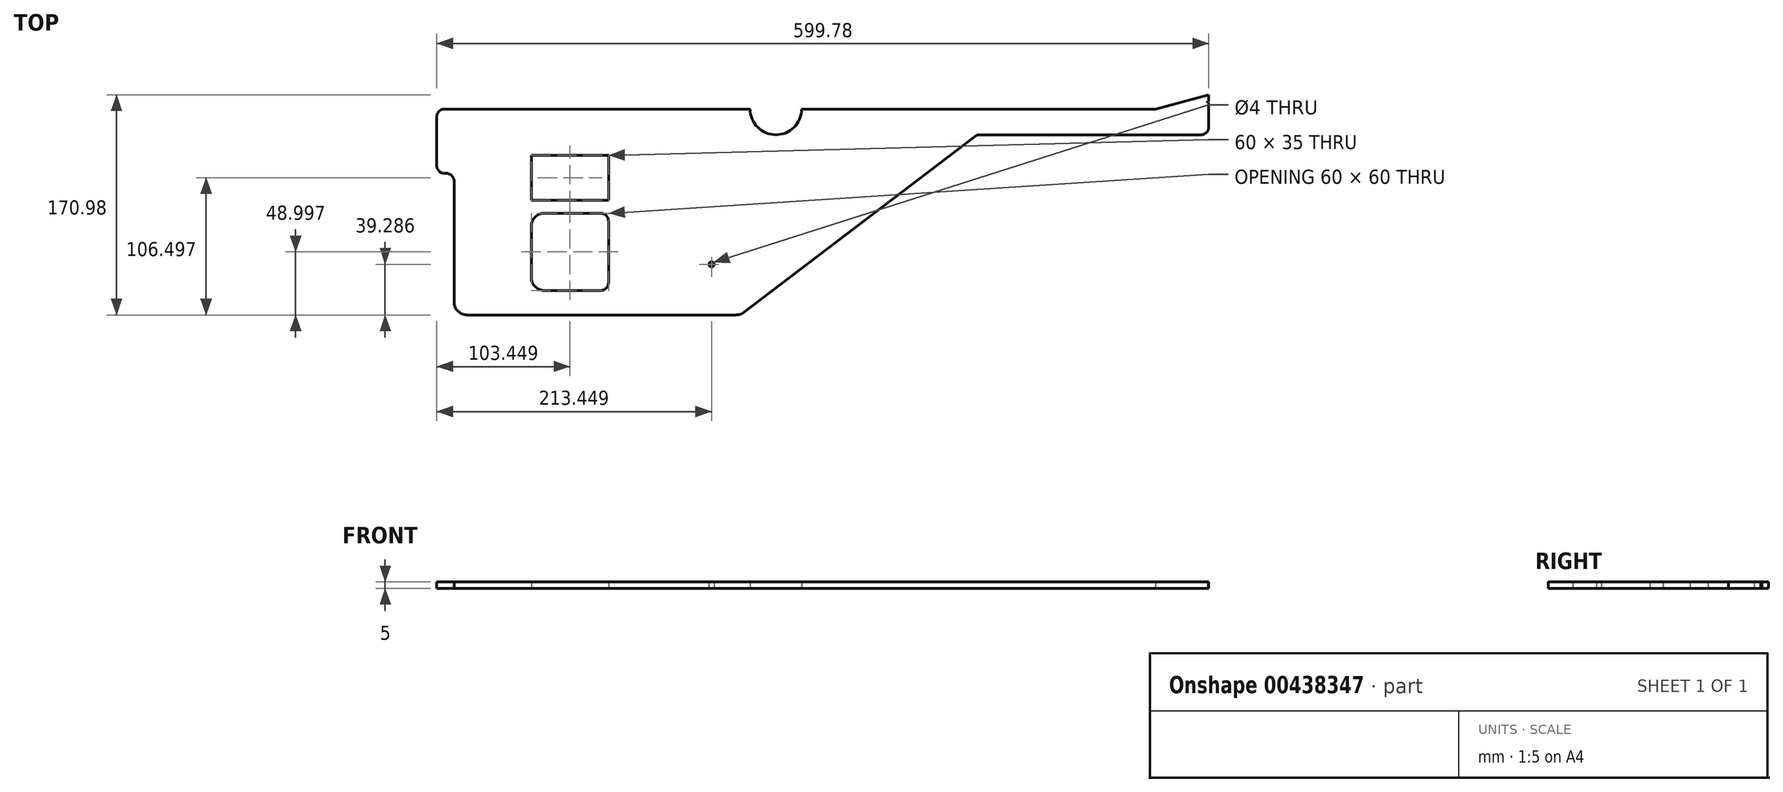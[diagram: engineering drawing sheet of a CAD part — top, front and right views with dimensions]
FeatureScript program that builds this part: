
annotation { "Feature Type Name" : "Feature", "Feature Type Description" : "" }
export const myFeature = defineFeature(function(context is Context, id is Id, definition is map)
    precondition{}
    {
        {
            var Q0;
            Q0=qCreatedBy(makeId("Top.planeOp"),FACE);
            var sketch = newSketch(context, id + "F0", { "sketchPlane" : qUnion([Q0])});
            skLineSegment(sketch, "E0", {"start": v(380.94, 53.83) * mm, "end": v(379.94, 53.83) * mm});
            skLineSegment(sketch, "E1", {"start": v(379.94, 53.83) * mm, "end": v(379.94, 54.83) * mm});
            skLineSegment(sketch, "E2", {"start": v(379.94, 54.83) * mm, "end": v(380.94, 54.83) * mm});
            skLineSegment(sketch, "E3", {"start": v(380.94, 54.83) * mm, "end": v(380.94, 59.83) * mm});
            skPoint(sketch, "E4", {"position": v(339.6, 48.83) * mm});
            skLineSegment(sketch, "E5", {"start": v(339.6, 48.83) * mm, "end": v(380.94, 59.83) * mm});
            skLineSegment(sketch, "E6", {"start": v(380.94, 53.83) * mm, "end": v(380.94, 34.83) * mm});
            skLineSegment(sketch, "E7", {"start": v(374.94, 28.83) * mm, "end": v(202.97, 28.83) * mm});
            skLineSegment(sketch, "E8", {"start": v(20, -109.1) * mm, "end": v(199.33, 27.6) * mm});
            skPoint(sketch, "E9.visualSharp", {"position": v(-218.84, 48.85) * mm});
            skPoint(sketch, "E10.visualSharp", {"position": v(17.31, -111.15) * mm});
            skArc(sketch, "E10.filletArc", {"start": v(13.94, -111.15) * mm, "mid": v(17.14, -110.63) * mm, "end": v(20, -109.1) * mm});
            skPoint(sketch, "E11.visualSharp", {"position": v(200.94, 28.83) * mm});
            skArc(sketch, "E11.filletArc", {"start": v(202.97, 28.83) * mm, "mid": v(201.05, 28.52) * mm, "end": v(199.33, 27.6) * mm});
            skPoint(sketch, "E12.visualSharp", {"position": v(380.94, 28.83) * mm});
            skArc(sketch, "E12.filletArc", {"start": v(374.94, 28.83) * mm, "mid": v(379.18, 30.6) * mm, "end": v(380.94, 34.83) * mm});
            skPoint(sketch, "E13", {"position": v(-5.4, -71.86) * mm});
            skCircle(sketch, "E14", {"center": v(-5.4, -71.86) * mm, "radius": 2 * mm});
            skPoint(sketch, "E15.visualSharp", {"position": v(20.24, -108.22) * mm});
            skLineSegment(sketch, "E16.bottom", {"start": v(-91.4, 12.85) * mm, "end": v(-145.4, 12.85) * mm});
            skLineSegment(sketch, "E16.top", {"start": v(-85.4, -22.15) * mm, "end": v(-145.4, -22.15) * mm});
            skLineSegment(sketch, "E16.left", {"start": v(-85.4, 6.85) * mm, "end": v(-85.4, -22.15) * mm});
            skLineSegment(sketch, "E16.right", {"start": v(-145.4, 12.85) * mm, "end": v(-145.4, -22.15) * mm});
            skLineSegment(sketch, "E17.bottom", {"start": v(-85.4, 12.85) * mm, "end": v(-145.4, 12.85) * mm});
            skLineSegment(sketch, "E17.top", {"start": v(-91.4, -22.15) * mm, "end": v(-145.4, -22.15) * mm});
            skLineSegment(sketch, "E17.left", {"start": v(-85.4, 12.85) * mm, "end": v(-85.4, -16.15) * mm});
            skArc(sketch, "E18.filletArc", {"start": v(-212.84, 48.85) * mm, "mid": v(-217.08, 47.09) * mm, "end": v(-218.84, 42.85) * mm});
            skArc(sketch, "E19", {"start": v(24.6, 48.84) * mm, "mid": v(44.6, 28.85) * mm, "end": v(64.6, 48.84) * mm});
            skLineSegment(sketch, "E20", {"start": v(-212.84, 48.85) * mm, "end": v(24.6, 48.84) * mm});
            skLineSegment(sketch, "E21", {"start": v(64.6, 48.84) * mm, "end": v(339.6, 48.83) * mm});
            skLineSegment(sketch, "E22.bottom", {"start": v(-91.4, -32.15) * mm, "end": v(-135.4, -32.15) * mm});
            skLineSegment(sketch, "E22.top", {"start": v(-91.4, -92.15) * mm, "end": v(-135.4, -92.15) * mm});
            skLineSegment(sketch, "E22.left", {"start": v(-85.4, -38.15) * mm, "end": v(-85.4, -86.15) * mm});
            skLineSegment(sketch, "E22.right", {"start": v(-145.4, -42.15) * mm, "end": v(-145.4, -82.15) * mm});
            skLineSegment(sketch, "E23", {"start": v(13.94, -111.15) * mm, "end": v(-195.4, -111.15) * mm});
            skLineSegment(sketch, "E24", {"start": v(-205.4, -101.15) * mm, "end": v(-205.4, -7.15) * mm});
            skLineSegment(sketch, "E25", {"start": v(-218.84, 42.85) * mm, "end": v(-218.84, 4.85) * mm});
            skLineSegment(sketch, "E26", {"start": v(-212.84, -1.15) * mm, "end": v(-211.4, -1.15) * mm});
            skPoint(sketch, "E27.visualSharp", {"position": v(-205.4, -1.15) * mm});
            skArc(sketch, "E27.filletArc", {"start": v(-205.4, -7.15) * mm, "mid": v(-207.15, -2.91) * mm, "end": v(-211.4, -1.15) * mm});
            skPoint(sketch, "E28.visualSharp", {"position": v(-218.84, -1.15) * mm});
            skArc(sketch, "E28.filletArc", {"start": v(-218.84, 4.85) * mm, "mid": v(-217.08, 0.6) * mm, "end": v(-212.84, -1.15) * mm});
            skPoint(sketch, "E29.visualSharp", {"position": v(-205.4, -111.15) * mm});
            skArc(sketch, "E29.filletArc", {"start": v(-205.4, -101.15) * mm, "mid": v(-202.46, -108.22) * mm, "end": v(-195.4, -111.15) * mm});
            skPoint(sketch, "E30.visualSharp", {"position": v(-145.4, -32.15) * mm});
            skArc(sketch, "E30.filletArc", {"start": v(-135.4, -32.15) * mm, "mid": v(-142.46, -35.08) * mm, "end": v(-145.4, -42.15) * mm});
            skPoint(sketch, "E31.visualSharp", {"position": v(-145.4, -92.15) * mm});
            skArc(sketch, "E31.filletArc", {"start": v(-145.4, -82.15) * mm, "mid": v(-142.46, -89.22) * mm, "end": v(-135.4, -92.15) * mm});
            skPoint(sketch, "E32.visualSharp", {"position": v(-85.4, -32.15) * mm});
            skArc(sketch, "E32.filletArc", {"start": v(-85.4, -38.15) * mm, "mid": v(-87.15, -33.91) * mm, "end": v(-91.4, -32.15) * mm});
            skPoint(sketch, "E33.visualSharp", {"position": v(-85.4, -92.15) * mm});
            skArc(sketch, "E33.filletArc", {"start": v(-91.4, -92.15) * mm, "mid": v(-87.15, -90.4) * mm, "end": v(-85.4, -86.15) * mm});
            skPoint(sketch, "E34.visualSharp", {"position": v(-85.4, 12.85) * mm});
            skArc(sketch, "E34.filletArc", {"start": v(-85.4, 6.85) * mm, "mid": v(-87.15, 11.09) * mm, "end": v(-91.4, 12.85) * mm});
            skPoint(sketch, "E35.visualSharp", {"position": v(-85.4, -22.15) * mm});
            skArc(sketch, "E35.filletArc", {"start": v(-91.4, -22.15) * mm, "mid": v(-87.15, -20.4) * mm, "end": v(-85.4, -16.15) * mm});
            skSolve(sketch);
        }
        {
            var Q0;
            Q0 = qSketchRegion(id + "F0", true);
            extrude(context, id + "F1", {"entities" : qUnion([Q0]), "depth" : 5 * mm});
        }
    });
